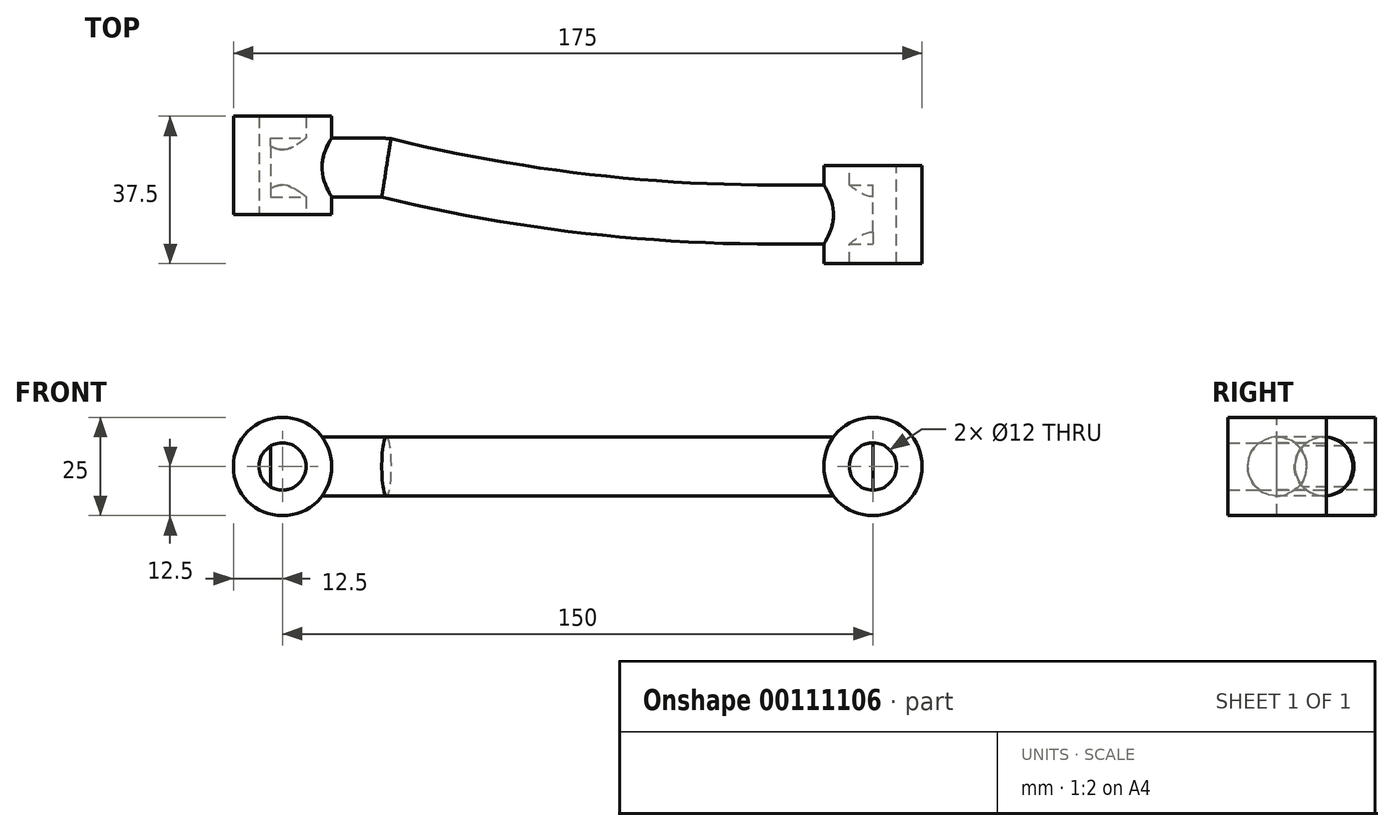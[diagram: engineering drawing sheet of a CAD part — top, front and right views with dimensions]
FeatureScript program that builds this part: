
annotation { "Feature Type Name" : "Feature", "Feature Type Description" : "" }
export const myFeature = defineFeature(function(context is Context, id is Id, definition is map)
    precondition{}
    {
        {
            var Q0;
            Q0=qCreatedBy(makeId("Front.planeOp"),FACE);
            var sketch = newSketch(context, id + "F0", { "sketchPlane" : qUnion([Q0])});
            skCircle(sketch, "E0", {"center": v(0, 0) * mm, "radius": 6 * mm});
            skCircle(sketch, "E1", {"center": v(0, 0) * mm, "radius": 12.5 * mm});
            skLineSegment(sketch, "E2", {"start": v(0, 0) * mm, "end": v(150, 0) * mm, "construction": true});
            skCircle(sketch, "E3", {"center": v(150, 0) * mm, "radius": 6 * mm});
            skCircle(sketch, "E4", {"center": v(150, 0) * mm, "radius": 12.5 * mm});
            skSolve(sketch);
        }
        {
            var Q0;
            Q0=makeQuery(id+"F0.imprint","IMPRINT",FACE,{"disambiguationData":[TD([[makeQuery(id+"F0.imprint","IMPRINT",EDGE,{"derivedFrom":sQuery(id+"F0.wireOp",EDGE,"E0")}),-1.0]])]});
            extrude(context, id + "F1", {"entities" : qUnion([Q0]), "oppositeDirection" : true, "depth" : 25 * mm});
        }
        {
            var Q0;
            Q0=qCreatedBy(makeId("Top.planeOp"),FACE);
            var sketch = newSketch(context, id + "F2", { "sketchPlane" : qUnion([Q0])});
            skLineSegment(sketch, "E5", {"start": v(-2.98, 12) * mm, "end": v(22.02, 12) * mm});
            skArc(sketch, "E6", {"start": v(26.36, 11.84) * mm, "mid": v(24.2, 11.96) * mm, "end": v(22.02, 12) * mm});
            skArc(sketch, "E7", {"start": v(26.36, 11.84) * mm, "mid": v(75.33, 2.97) * mm, "end": v(125, 0) * mm});
            skLineSegment(sketch, "E8", {"start": v(125, 0) * mm, "end": v(150, 0) * mm});
            skSolve(sketch);
        }
        {
            var Q0;
            Q0=qCreatedBy(makeId("Right.planeOp"),FACE);
            var sketch = newSketch(context, id + "F3", { "sketchPlane" : qUnion([Q0])});
            skCircle(sketch, "E9", {"center": v(12, 0) * mm, "radius": 7.5 * mm});
            skSolve(sketch);
        }
        {
            var Q0;
            Q0 = qSketchRegion(id + "F3", true);
            var Q1;
            Q1 = qConstructionFilter(qBodyType(qCreatedBy(id + "F2" ,EDGE), BodyType.WIRE), ConstructionObject.NO);
            sweep(context, id + "F4", {"operationType" : NewBodyOperationType.ADD, "profiles" : qUnion([Q0]), "path" : qUnion([Q1])});
        }
        {
            var Q0;
            Q0=makeQuery(id+"F0.imprint","IMPRINT",FACE,{"disambiguationData":[TD([[makeQuery(id+"F0.imprint","IMPRINT",EDGE,{"derivedFrom":sQuery(id+"F0.wireOp",EDGE,"E3")}),-1.0]])]});
            extrude(context, id + "F5", {"entities" : qUnion([Q0]), "operationType" : NewBodyOperationType.ADD, "endBound" : BoundingType.SYMMETRIC, "depth" : 25 * mm});
        }
    });
